# Revit family: RME-Ceiling
name_source: partatom
category: Lighting Fixtures
revit_build: Autodesk Revit MEP 2012 (Build: 20110309_2315(x64)
units: mm (PartAtom-declared; Revit-internal decimal feet)

## types (3) — shared parameters
Color Filter = 16777215
Default Elevation = 48.000"
Description = Running Man Exit Sign
Dimming Lamp Color Temperature Shift = <None>
Emit Shape Visible in Rendering = No
Emit from Rectangle Length = 11.000"
Emit from Rectangle Width = 6.000"
Finish = Hubbell - White
Is 120VAC = Yes
Is 277VAC = No
Lamp = LED Lamp
Lens = Hubbell - Green Glass
Load Classification = Lighting
Manufacturer = Compass Lighting
Manufacturer Fax = 866-898-0131
Model = RME
Photometric Web File = generic
Product Documentation Link = http://cdn.compasslightingproducts.com
Product Page URL = http://www.compasslightingproducts.com
Tilt Angle = -90.00°
URL = http://www.compasslightingproducts.com
Voltage = 120 V

## per-type parameters (varying)
| type | Apparent Load | Watts |
| RMEUW | 3 VA | 3 W |
| RMEUWE | 2 VA | 2 W |
| RMEUWE-SD | 4 VA | 4 W |

## geometry (parser evidence)
native form markers: Blend x2, Sweep x3
no freeform markers — native parametric forms only
